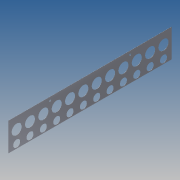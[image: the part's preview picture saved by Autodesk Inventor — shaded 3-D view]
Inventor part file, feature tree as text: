
AUTODESK INVENTOR PART (.ipt)
format: ipt  version: 2014 SP1 (Build 180222100, 222)  size: 227,328 bytes
history: native  units: in
note: dims shown in document units (in); Inventor stores cm internally (conversion verified against a paired STEP export)
features: sketch x5, hole x4, other x2, thicken_offset x1, sheet_metal_op x1, extrude x1
ambient origin geometry x8: Origin, YZ Plane, XZ Plane, XY Plane, X Axis, Y Axis, Z Axis, Center Point
bodies: Solid1 (feature_tree)
feature tree (14):
  thicken_offset  "Thicken1"
  sheet_metal_op  "Unfold4"
  hole  "spars"  [1 undecoded]
  hole  "supports"  [1 undecoded]
  hole  "rivets"  [1 undecoded]
  hole  "rebar"  [1 undecoded]
  sketch  "Sketch1"  dims[d0=0.0in d1=144.2386in d2=10.0in d3=0.0in]
  other  "2D Equation Curve1"
  other  "Srf1"
  sketch  "Sketch2"  dims[d4=0.0394in d5=0.0394in]
  sketch  "Sketch3"  dims[d6=3.622in d7=5.9055in]
  sketch  "Sketch7"  dims[d8=2.905in d9=4.7244in d11=4.7124in d12=0.3937in d14=1.0in]
  sketch  "Sketch9"  dims[d16=3.5827in d17=0.75in d18=0.375in d19=0.25in d20=0.5635in d21=0.0394in d22=0.8108in d23=2.4803in d24=1.5748in d25=4.7244in d27=4.7125in d28=0.3937in d30=1.0in d32=2.905in d33=2.5197in d34=0.75in d35=0.375in d36=0.25in d37=0.5635in d38=0.0394in d39=0.8108in d68=0.125in d69=1.0in d70=0.5in d71=1.9685in d73=2.0in d74=0.3937in d76=1.0in d78=1.0in d79=0.0394in d80=0.75in d81=0.375in d82=0.25in d83=0.5635in d84=0.0394in d85=0.8108in d88=0.3937in d89=0.5906in d90=0.75in d91=0.375in d92=0.25in d93=0.5635in d94=0.0394in d95=0.8108in d101=2.8386in d102=1.2559in]
  extrude  "ExtrusionSrf1"  Depth=0.8108in
note: 4 required parameter values undecoded (feature->parameter linkage not recoverable at this tier; creation-order binding heuristic only, values carry confidence <= 0.55)
